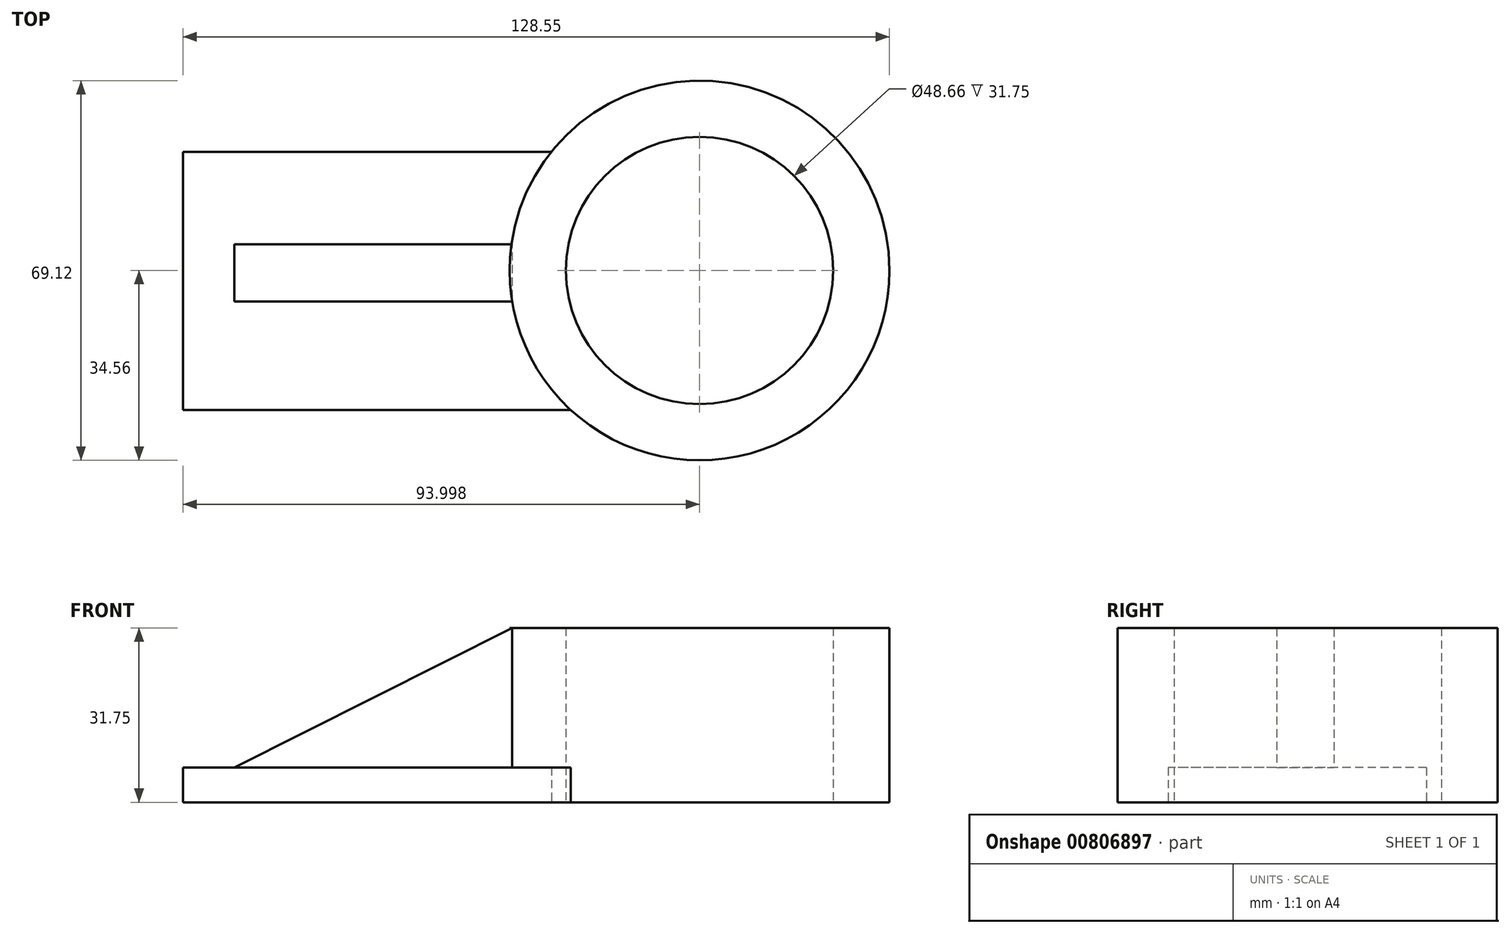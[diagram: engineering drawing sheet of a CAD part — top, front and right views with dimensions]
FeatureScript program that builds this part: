
annotation { "Feature Type Name" : "Feature", "Feature Type Description" : "" }
export const myFeature = defineFeature(function(context is Context, id is Id, definition is map)
    precondition{}
    {
        {
            var Q0;
            Q0=qCreatedBy(makeId("Top.planeOp"),FACE);
            var sketch = newSketch(context, id + "F0", { "sketchPlane" : qUnion([Q0])});
            skCircle(sketch, "E0", {"center": v(33.88, 0) * mm, "radius": 34.56 * mm});
            skCircle(sketch, "E1", {"center": v(33.88, 0) * mm, "radius": 24.33 * mm});
            skSolve(sketch);
        }
        {
            var Q0;
            Q0=makeQuery(id+"F0.imprint","IMPRINT",FACE,{"disambiguationData":[TD([[makeQuery(id+"F0.imprint","IMPRINT",EDGE,{"derivedFrom":sQuery(id+"F0.wireOp",EDGE,"E0")}),1.0]])]});
            extrude(context, id + "F1", {"entities" : qUnion([Q0]), "depth" : 50.8 * mm, "offsetDistance" : 25.4 * mm});
        }
        {
            var Q0;
            Q0=qCreatedBy(makeId("Top.planeOp"),FACE);
            var sketch = newSketch(context, id + "F2", { "sketchPlane" : qUnion([Q0])});
            skLineSegment(sketch, "E2.bottom", {"start": v(14.27, 21.62) * mm, "end": v(-60.12, 21.62) * mm});
            skLineSegment(sketch, "E2.top", {"start": v(14.27, -25.37) * mm, "end": v(-60.12, -25.37) * mm});
            skLineSegment(sketch, "E2.left", {"start": v(14.27, 21.62) * mm, "end": v(14.27, -25.37) * mm});
            skLineSegment(sketch, "E2.right", {"start": v(-60.12, 21.62) * mm, "end": v(-60.12, -25.37) * mm});
            skSolve(sketch);
        }
        {
            var Q0;
            Q0=makeQuery(id+"F2.imprint","IMPRINT",FACE,{"disambiguationData":[TD([[makeQuery(id+"F2.imprint","IMPRINT",EDGE,{"derivedFrom":sQuery(id+"F2.wireOp",EDGE,"E2.bottom")}),1.0]])]});
            extrude(context, id + "F3", {"entities" : qUnion([Q0]), "operationType" : NewBodyOperationType.ADD, "depth" : 25.4 * mm, "offsetDistance" : 25.4 * mm});
        }
        {
            var Q0;
            Q0=makeQuery(id+"F1.opExtrude","CAP_FACE",FACE,{"disambiguationData":[OSD([sQuery(id+"F0.wireOp",EDGE,"E0"),sQuery(id+"F0.wireOp",EDGE,"E1")])],"isStart":false});
            extrude(context, id + "F4", {"entities" : qUnion([Q0]), "operationType" : NewBodyOperationType.REMOVE, "oppositeDirection" : true, "depth" : 19.05 * mm, "offsetDistance" : 25.4 * mm});
        }
        {
            var Q0;
            {var subQ0=sQuery(id+"F2.wireOp",EDGE,"E2.bottom");var subQ1=sQuery(id+"F2.wireOp",EDGE,"E2.right");var subQ2=sQuery(id+"F2.wireOp",EDGE,"E2.top");Q0=makeQuery(id+"F3.boolean.opBoolean","SPLIT",FACE,{"disambiguationData":[TD([makeQuery(id+"F1.opExtrude","SWEPT_FACE",FACE,{"disambiguationData":[OSD([sQuery(id+"F0.wireOp",EDGE,"E0")])]})])],"derivedFrom":makeQuery(id+"F3.opExtrude","CAP_FACE",FACE,{"disambiguationData":[OSD([subQ0,subQ2,sQuery(id+"F2.wireOp",EDGE,"E2.left"),subQ1])],"isStart":false})});}
            extrude(context, id + "F5", {"entities" : qUnion([Q0]), "operationType" : NewBodyOperationType.REMOVE, "oppositeDirection" : true, "depth" : 19.05 * mm, "offsetDistance" : 25.4 * mm});
        }
        {
            var Q0;
            {var subQ0=sQuery(id+"F2.wireOp",EDGE,"E2.left");Q0=makeQuery(id+"F3.boolean.opBoolean","SPLIT",FACE,{"disambiguationData":[TD([makeQuery(id+"F1.opExtrude","SWEPT_FACE",FACE,{"disambiguationData":[OSD([sQuery(id+"F0.wireOp",EDGE,"E1")])]})])],"derivedFrom":makeQuery(id+"F3.opExtrude","CAP_FACE",FACE,{"disambiguationData":[OSD([sQuery(id+"F2.wireOp",EDGE,"E2.bottom"),sQuery(id+"F2.wireOp",EDGE,"E2.top"),subQ0,sQuery(id+"F2.wireOp",EDGE,"E2.right")])],"isStart":false})});}
            extrude(context, id + "F6", {"entities" : qUnion([Q0]), "operationType" : NewBodyOperationType.REMOVE, "oppositeDirection" : true, "depth" : 50.8 * mm, "offsetDistance" : 25.4 * mm});
        }
        {
            var Q0;
            Q0=qCreatedBy(makeId("Right.planeOp"),FACE);
            var sketch = newSketch(context, id + "F7", { "sketchPlane" : qUnion([Q0])});
            skLineSegment(sketch, "E3.bottom", {"start": v(4.76, 31.72) * mm, "end": v(-5.62, 31.72) * mm});
            skLineSegment(sketch, "E3.top", {"start": v(4.76, 5.77) * mm, "end": v(-5.62, 5.77) * mm});
            skLineSegment(sketch, "E3.left", {"start": v(4.76, 31.72) * mm, "end": v(4.76, 5.77) * mm});
            skLineSegment(sketch, "E3.right", {"start": v(-5.62, 31.72) * mm, "end": v(-5.62, 5.77) * mm});
            skSolve(sketch);
        }
        {
            var Q0;
            Q0 = qSketchRegion(id + "F7", true);
            extrude(context, id + "F8", {"entities" : qUnion([Q0]), "operationType" : NewBodyOperationType.ADD, "oppositeDirection" : true, "depth" : 50.8 * mm, "offsetDistance" : 25.4 * mm});
        }
        {
            var Q0;
            Q0=makeQuery(id+"F8.opExtrude","SWEPT_FACE",FACE,{"disambiguationData":[OSD([sQuery(id+"F7.wireOp",EDGE,"E3.right")])]});
            var sketch = newSketch(context, id + "F9", { "sketchPlane" : qUnion([Q0])});
            skLineSegment(sketch, "E4", {"start": v(-0.22, 31.72) * mm, "end": v(-50.8, 6.35) * mm});
            skLineSegment(sketch, "E5", {"start": v(-50.8, 6.35) * mm, "end": v(-67.8, 40.27) * mm});
            skLineSegment(sketch, "E6", {"start": v(-67.8, 40.27) * mm, "end": v(-0.22, 31.72) * mm});
            skSolve(sketch);
        }
        {
            var Q0;
            Q0=makeQuery(id+"F9.imprint","IMPRINT",FACE,{"disambiguationData":[TD([[makeQuery(id+"F9.imprint","IMPRINT",EDGE,{"derivedFrom":sQuery(id+"F9.wireOp",EDGE,"E4")}),-1.0]])]});
            extrude(context, id + "F10", {"entities" : qUnion([Q0]), "operationType" : NewBodyOperationType.REMOVE, "oppositeDirection" : true, "depth" : 76.2 * mm, "offsetDistance" : 25.4 * mm});
        }
    });
